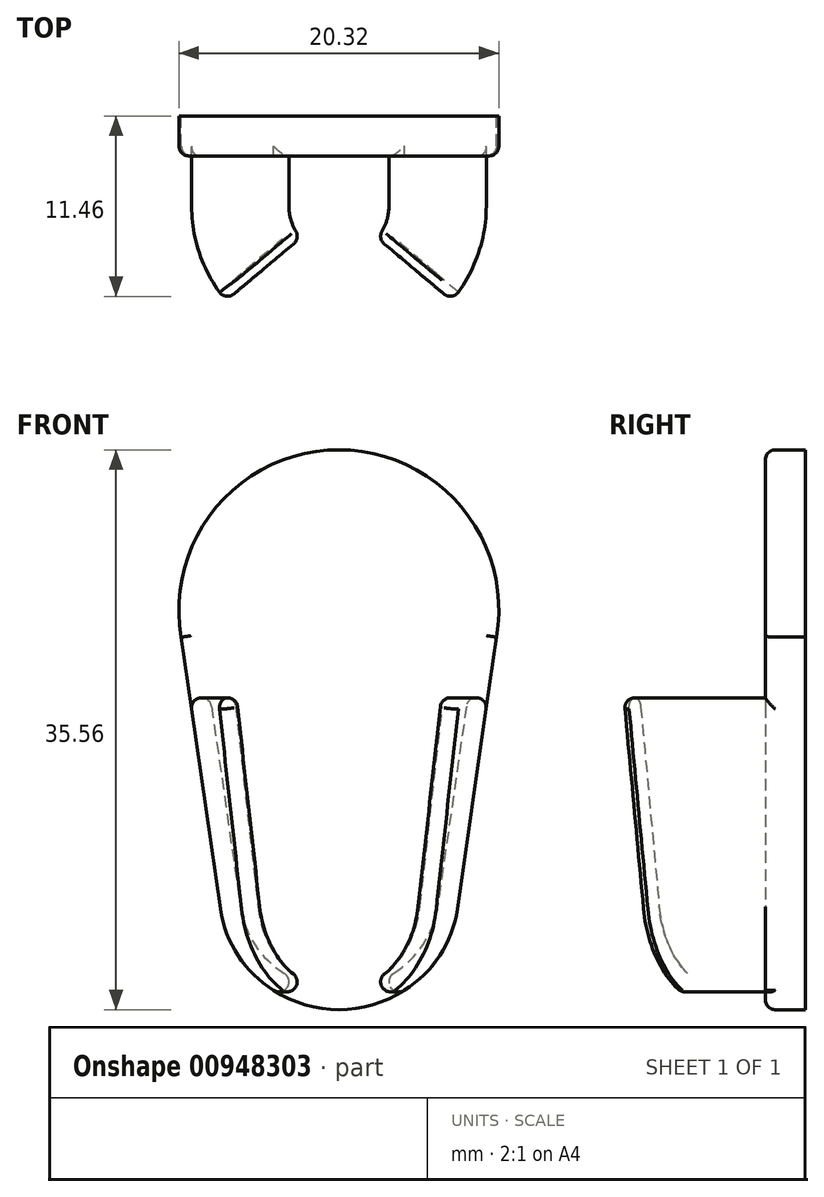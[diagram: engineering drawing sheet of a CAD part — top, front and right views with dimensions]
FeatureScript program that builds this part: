
annotation { "Feature Type Name" : "Feature", "Feature Type Description" : "" }
export const myFeature = defineFeature(function(context is Context, id is Id, definition is map)
    precondition{}
    {
        {
            var Q0;
            Q0=qCreatedBy(makeId("Front.planeOp"),FACE);
            var sketch = newSketch(context, id + "F0", { "sketchPlane" : qUnion([Q0])});
            skCircle(sketch, "E0", {"center": v(0, 10.16) * mm, "radius": 10.16 * mm});
            skCircle(sketch, "E1", {"center": v(0, -7.62) * mm, "radius": 7.62 * mm});
            skLineSegment(sketch, "E2", {"start": v(10, 8.42) * mm, "end": v(7.54, -8.7) * mm});
            skLineSegment(sketch, "E3.MirrorCS", {"start": v(-10, 8.42) * mm, "end": v(-7.54, -8.7) * mm});
            skLineSegment(sketch, "E4", {"start": v(0, 20.32) * mm, "end": v(0, -15.24) * mm, "construction": true});
            skPoint(sketch, "E5", {"position": v(0, 2.54) * mm});
            skSolve(sketch);
        }
        {
            var Q0;
            {var subQ0=sQuery(id+"F0.wireOp",EDGE,"E2");var subQ1=sQuery(id+"F0.wireOp",EDGE,"E0");var subQ2=makeQuery(id+"F0.imprint","INTERSECT",VERTEX,{"disambiguationData":[OD(0.0)],"derivedFrom":[subQ1,subQ0]});Q0=makeQuery(id+"F0.imprint","IMPRINT",FACE,{"disambiguationData":[TD([[makeQuery(id+"F0.imprint","IMPRINT",EDGE,{"disambiguationData":[TD([[subQ2,-1.0]])],"derivedFrom":subQ1}),1.0]])]});}
            var Q1;
            {var subQ0=sQuery(id+"F0.wireOp",EDGE,"E1");var subQ1=makeQuery(id+"F0.imprint","INTERSECT",VERTEX,{"derivedFrom":[subQ0,sQuery(id+"F0.wireOp",EDGE,"E33TimzY-OEYj-ruqF-KgCk-srEfJ6886ytW")]});Q1=makeQuery(id+"F0.imprint","IMPRINT",FACE,{"disambiguationData":[TD([[makeQuery(id+"F0.imprint","IMPRINT",EDGE,{"disambiguationData":[TD([[subQ1,1.0]])],"derivedFrom":subQ0}),1.0]])]});}
            var Q2;
            {var subQ0=sQuery(id+"F0.wireOp",EDGE,"E2");var subQ1=sQuery(id+"F0.wireOp",EDGE,"E0");var subQ2=makeQuery(id+"F0.imprint","INTERSECT",VERTEX,{"disambiguationData":[OD(1.0)],"derivedFrom":[subQ1,subQ0]});Q2=makeQuery(id+"F0.imprint","IMPRINT",FACE,{"disambiguationData":[TD([[makeQuery(id+"F0.imprint","IMPRINT",EDGE,{"disambiguationData":[TD([[subQ2,1.0]])],"derivedFrom":subQ1}),-1.0]])]});}
            var Q3;
            {var subQ0=sQuery(id+"F0.wireOp",EDGE,"E33TimzY-OEYj-ruqF-KgCk-srEfJ6886ytW");var subQ1=sQuery(id+"F0.wireOp",EDGE,"E0");var subQ2=makeQuery(id+"F0.imprint","INTERSECT",VERTEX,{"disambiguationData":[OD(1.0)],"derivedFrom":[subQ1,subQ0]});Q3=makeQuery(id+"F0.imprint","IMPRINT",FACE,{"disambiguationData":[TD([[makeQuery(id+"F0.imprint","IMPRINT",EDGE,{"disambiguationData":[TD([[subQ2,-1.0]])],"derivedFrom":subQ1}),-1.0]])]});}
            extrude(context, id + "F1", {"entities" : qUnion([Q0, Q1, Q2, Q3]), "depth" : 2.54 * mm, "offsetDistance" : 25.4 * mm});
        }
        {
            var Q0;
            Q0=makeQuery(id+"F1.opExtrude","CAP_FACE",FACE,{"disambiguationData":[OSD([sQuery(id+"F0.wireOp",EDGE,"E0"),sQuery(id+"F0.wireOp",EDGE,"E1"),sQuery(id+"F0.wireOp",EDGE,"E2"),sQuery(id+"F0.wireOp",EDGE,"E3.MirrorCS")])],"isStart":false});
            var sketch = newSketch(context, id + "F2", { "sketchPlane" : qUnion([Q0])});
            skCircle(sketch, "E6", {"center": v(-8.72, 3.94) * mm, "radius": 0.64 * mm});
            skLineSegment(sketch, "E7", {"start": v(10, 8.42) * mm, "end": v(7.54, -8.7) * mm});
            skArc(sketch, "E8", {"start": v(10, 8.42) * mm, "mid": v(0, 20.32) * mm, "end": v(-10, 8.42) * mm});
            skLineSegment(sketch, "E9", {"start": v(-5.5, -13.38) * mm, "end": v(-5.5, -13.38) * mm});
            skCircle(sketch, "E10", {"center": v(-6.9, -8.76) * mm, "radius": 0.64 * mm});
            skCircle(sketch, "E11", {"center": v(-3.81, -13.47) * mm, "radius": 0.64 * mm});
            skLineSegment(sketch, "E12", {"start": v(-8.1, 4.03) * mm, "end": v(-6.26, -8.67) * mm});
            skLineSegment(sketch, "E13", {"start": v(-9.35, 3.85) * mm, "end": v(-7.52, -8.85) * mm});
            skArc(sketch, "E14", {"start": v(-7.52, -8.85) * mm, "mid": v(-6.4, -11.8) * mm, "end": v(-4.14, -14.01) * mm});
            skArc(sketch, "E15", {"start": v(-6.26, -8.67) * mm, "mid": v(-5.34, -11.11) * mm, "end": v(-3.48, -12.93) * mm});
            skCircle(sketch, "E16.MirrorC", {"center": v(6.9, -8.76) * mm, "radius": 0.64 * mm});
            skCircle(sketch, "E17.MirrorC", {"center": v(8.72, 3.94) * mm, "radius": 0.64 * mm});
            skCircle(sketch, "E18.MirrorC", {"center": v(3.81, -13.47) * mm, "radius": 0.64 * mm});
            skLineSegment(sketch, "E19.MirrorCS", {"start": v(9.35, 3.85) * mm, "end": v(7.52, -8.85) * mm});
            skLineSegment(sketch, "E20.MirrorCS", {"start": v(8.1, 4.03) * mm, "end": v(6.26, -8.67) * mm});
            skArc(sketch, "E21.MirrorCS", {"start": v(7.52, -8.85) * mm, "mid": v(6.4, -11.8) * mm, "end": v(4.14, -14.01) * mm});
            skArc(sketch, "E22.MirrorCS", {"start": v(6.26, -8.67) * mm, "mid": v(5.34, -11.11) * mm, "end": v(3.48, -12.93) * mm});
            skLineSegment(sketch, "E23", {"start": v(0, 20.32) * mm, "end": v(0, -15.24) * mm, "construction": true});
            skLineSegment(sketch, "E24", {"start": v(-7.53, -8.76) * mm, "end": v(7.53, -8.76) * mm, "construction": true});
            skSolve(sketch);
        }
        {
            var Q0;
            Q0 = qSketchRegion(id + "F2", true);
            extrude(context, id + "F3", {"entities" : qUnion([Q0]), "operationType" : NewBodyOperationType.ADD, "depth" : 3.17 * mm, "offsetDistance" : 25.4 * mm});
        }
        {
            var Q0;
            Q0=makeQuery(id+"F3.opExtrude","CAP_FACE",FACE,{"disambiguationData":[OSD([sQuery(id+"F2.wireOp",EDGE,"E6"),sQuery(id+"F2.wireOp",EDGE,"E11"),sQuery(id+"F2.wireOp",EDGE,"E12"),sQuery(id+"F2.wireOp",EDGE,"E13"),sQuery(id+"F2.wireOp",EDGE,"E14"),sQuery(id+"F2.wireOp",EDGE,"E15")])],"isStart":false});
            var sketch = newSketch(context, id + "F4", { "sketchPlane" : qUnion([Q0])});
            skLineSegment(sketch, "E25", {"start": v(0, -16.6) * mm, "end": v(0, 4.8) * mm, "construction": true});
            skSolve(sketch);
        }
        {
            var Q0;
            Q0=makeQuery(id+"F4.imprint","IMPRINT",FACE,{"disambiguationData":[TD([[makeQuery(id+"F4.imprint","IMPRINT",EDGE,{"derivedFrom":makeQuery(id+"F3.opExtrude","CAP_EDGE",EDGE,{"disambiguationData":[OSD([sQuery(id+"F2.wireOp",EDGE,"E6")])],"isStart":false})}),1.0]])]});
            var Q1;
            Q1=sQuery(id+"F4.wireOp",EDGE,"E25");
            var Q2;
            Q2=sQuery(id+"F4.wireOp",EDGE,"E25");
            revolve(context, id + "F5", {"operationType" : NewBodyOperationType.ADD, "surfaceOperationType" : NewSurfaceOperationType.NEW, "entities" : qUnion([Q0]), "surfaceEntities" : qUnion([Q1]), "axis" : qUnion([Q2]), "revolveType" : RevolveType.ONE_DIRECTION, "angle" : 40 * degree});
        }
        {
            var Q0;
            Q0=makeQuery(id+"F3.opExtrude","CAP_FACE",FACE,{"disambiguationData":[OSD([sQuery(id+"F2.wireOp",EDGE,"E17.MirrorC"),sQuery(id+"F2.wireOp",EDGE,"E18.MirrorC"),sQuery(id+"F2.wireOp",EDGE,"E19.MirrorCS"),sQuery(id+"F2.wireOp",EDGE,"E20.MirrorCS"),sQuery(id+"F2.wireOp",EDGE,"E21.MirrorCS"),sQuery(id+"F2.wireOp",EDGE,"E22.MirrorCS")])],"isStart":false});
            var Q1;
            Q1=sQuery(id+"F4.wireOp",EDGE,"E25");
            revolve(context, id + "F6", {"operationType" : NewBodyOperationType.ADD, "surfaceOperationType" : NewSurfaceOperationType.NEW, "entities" : qUnion([Q0]), "axis" : qUnion([Q1]), "revolveType" : RevolveType.ONE_DIRECTION, "oppositeDirection" : true, "angle" : 40 * degree});
        }
        {
            var Q0;
            Q0=makeQuery(id+"F1.opExtrude","CAP_EDGE",EDGE,{"disambiguationData":[OSD([sQuery(id+"F0.wireOp",EDGE,"E0")])],"isStart":false});
            var Q1;
            {var subQ0=sQuery(id+"F0.wireOp",EDGE,"E1");Q1=makeQuery(id+"F3.boolean.opBoolean","SPLIT",EDGE,{"disambiguationData":[topologyDisambiguationEdgeConnected([makeQuery(id+"F1.opExtrude","CAP_FACE",FACE,{"disambiguationData":[OSD([sQuery(id+"F0.wireOp",EDGE,"E0"),subQ0,sQuery(id+"F0.wireOp",EDGE,"E2"),sQuery(id+"F0.wireOp",EDGE,"E3.MirrorCS")])],"isStart":false})])],"derivedFrom":makeQuery(id+"F1.opExtrude","CAP_EDGE",EDGE,{"disambiguationData":[OSD([subQ0])],"isStart":false})});}
            fillet(context, id + "F7", {"entities" : qUnion([Q0, Q1]), "radius" : 0.64 * mm, "tangentPropagation" : true, "allowEdgeOverflow" : false});
        }
        {
            var Q0;
            Q0=makeQuery(id+"F6.opRevolve","CAP_FACE",FACE,{"disambiguationData":[OSD([sQuery(id+"F2.wireOp",EDGE,"E17.MirrorC"),sQuery(id+"F2.wireOp",EDGE,"E18.MirrorC"),sQuery(id+"F2.wireOp",EDGE,"E19.MirrorCS"),sQuery(id+"F2.wireOp",EDGE,"E20.MirrorCS"),sQuery(id+"F2.wireOp",EDGE,"E21.MirrorCS"),sQuery(id+"F2.wireOp",EDGE,"E22.MirrorCS")])],"isStart":false});
            var Q1;
            Q1=makeQuery(id+"F5.opRevolve","CAP_FACE",FACE,{"disambiguationData":[OSD([sQuery(id+"F2.wireOp",EDGE,"E6"),sQuery(id+"F2.wireOp",EDGE,"E11"),sQuery(id+"F2.wireOp",EDGE,"E12"),sQuery(id+"F2.wireOp",EDGE,"E13"),sQuery(id+"F2.wireOp",EDGE,"E14"),sQuery(id+"F2.wireOp",EDGE,"E15")])],"isStart":false});
            fillet(context, id + "F8", {"entities" : qUnion([Q0, Q1]), "radius" : 0.64 * mm, "tangentPropagation" : true, "allowEdgeOverflow" : false});
        }
    });
